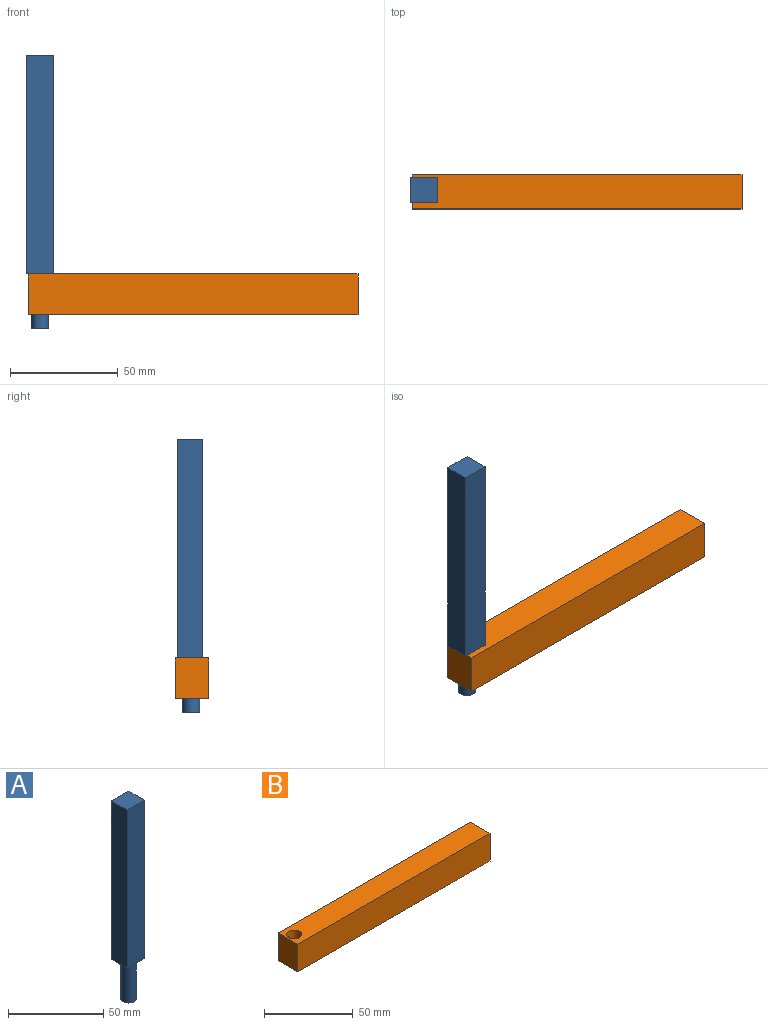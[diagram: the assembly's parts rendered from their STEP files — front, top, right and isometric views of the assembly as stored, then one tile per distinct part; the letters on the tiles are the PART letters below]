
ASSEMBLY  parts=2 mates=1
PART A: 8 faces, bbox 12.8x11.7x127 mm
  f0: plane 101.6x11.71mm, normal (-1,0,0), area 1189.9mm2, adj f1,f3,f4,f5
  f1: plane 101.6x12.82mm, normal (0,-1,0), area 1302.6mm2, adj f0,f2,f4,f5
  f2: plane 101.6x11.71mm, normal (1,0,0), area 1189.9mm2, adj f1,f3,f4,f5
  f3: plane 101.6x12.82mm, normal (0,1,0), area 1302.6mm2, adj f0,f2,f4,f5
  f4: plane 12.82x11.71mm, normal (0,0,1), area 150.2mm2, adj f0,f1,f2,f3
  f5: plane 12.82x11.71mm, normal (0,0,-1), area 99.5mm2, adj f0,f1,f2,f3,f6
  f6: cylinder r=4.01mm len=25.4mm, axis (0,0,1), area 640.6mm2, adj f5,f7
  f7: plane 8.03x8.03mm, normal (0,0,-1), area 50.6mm2, adj f6
PART B: 7 faces, bbox 153.4x15.8x19.1 mm
  f0: plane 19.05x15.78mm, normal (-1,0,0), area 300.6mm2, adj f1,f3,f4,f5
  f1: plane 153.36x19.05mm, normal (0,-1,0), area 2921.6mm2, adj f0,f2,f4,f5
  f2: plane 19.05x15.78mm, normal (1,0,0), area 300.6mm2, adj f1,f3,f4,f5
  f3: plane 153.36x19.05mm, normal (0,1,0), area 2921.6mm2, adj f0,f2,f4,f5
  f4: plane 153.36x15.78mm, normal (0,0,1), area 2363.7mm2, adj f0,f1,f2,f3,f6
  f5: plane 153.36x15.78mm, normal (0,0,-1), area 2363.7mm2, adj f0,f1,f2,f3,f6
  f6: cylinder r=4.24mm len=19.05mm, axis (0,0,-1), area 507.1mm2, adj f4,f5
PLACE A t=(-47.25,46.46,42.88)mm
PLACE B t=(8.23,40.17,23.83)mm
MATE revolute A.f6 <-> B.f6  axis (0,0,-1) through (-40.84,40.17,42.88)mm
